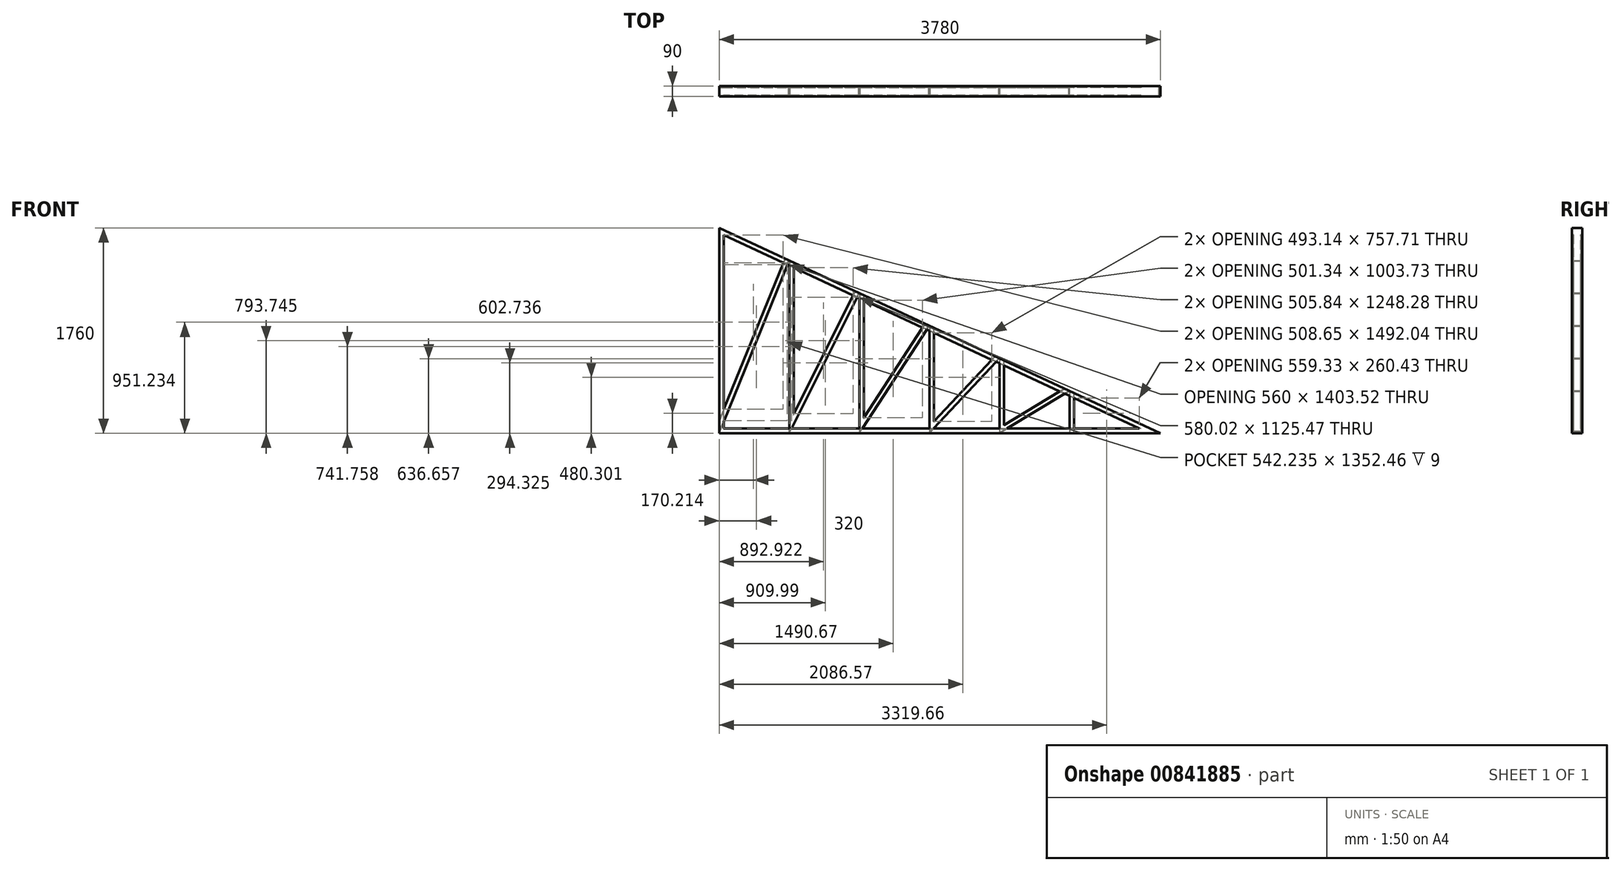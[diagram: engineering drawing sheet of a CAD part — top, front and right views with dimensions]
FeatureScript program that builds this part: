
annotation { "Feature Type Name" : "Feature", "Feature Type Description" : "" }
export const myFeature = defineFeature(function(context is Context, id is Id, definition is map)
    precondition{}
    {
        {
            var Q0;
            Q0=qCreatedBy(makeId("Front.planeOp"),FACE);
            var sketch = newSketch(context, id + "F0", { "sketchPlane" : qUnion([Q0])});
            skLineSegment(sketch, "E0", {"start": v(0, 0) * mm, "end": v(3780, 0) * mm});
            skLineSegment(sketch, "E1", {"start": v(3780, 0) * mm, "end": v(0, 1760) * mm});
            skLineSegment(sketch, "E2", {"start": v(0, 1760) * mm, "end": v(0, 0) * mm});
            skSolve(sketch);
        }
        {
            var Q0;
            Q0=qCreatedBy(makeId("Right.planeOp"),FACE);
            var sketch = newSketch(context, id + "F1", { "sketchPlane" : qUnion([Q0])});
            skLineSegment(sketch, "E3", {"start": v(0, 0) * mm, "end": v(-45, 0) * mm});
            skLineSegment(sketch, "E4", {"start": v(-45, 0) * mm, "end": v(-45, 40) * mm});
            skLineSegment(sketch, "E5", {"start": v(-45, 40) * mm, "end": v(-33, 40) * mm});
            skLineSegment(sketch, "E6.MirrorCS", {"start": v(45, 40) * mm, "end": v(33, 40) * mm});
            skLineSegment(sketch, "E7.MirrorCS", {"start": v(45, 0) * mm, "end": v(45, 40) * mm});
            skLineSegment(sketch, "E8.MirrorCS", {"start": v(0, 0) * mm, "end": v(45, 0) * mm});
            skLineSegment(sketch, "E9.0", {"start": v(-42, 37) * mm, "end": v(-33, 37) * mm});
            skLineSegment(sketch, "E9.1", {"start": v(-42, 3) * mm, "end": v(-42, 37) * mm});
            skLineSegment(sketch, "E9.2", {"start": v(42, 37) * mm, "end": v(33, 37) * mm});
            skLineSegment(sketch, "E9.3", {"start": v(42, 3) * mm, "end": v(42, 37) * mm});
            skLineSegment(sketch, "E9.4", {"start": v(0, 3) * mm, "end": v(42, 3) * mm});
            skLineSegment(sketch, "E9.5", {"start": v(0, 3) * mm, "end": v(-42, 3) * mm});
            skLineSegment(sketch, "E10", {"start": v(33, 40) * mm, "end": v(33, 37) * mm});
            skLineSegment(sketch, "E11", {"start": v(-33, 40) * mm, "end": v(-33, 37) * mm});
            skSolve(sketch);
        }
        {
            var Q0;
            Q0 = qSketchRegion(id + "F1", true);
            var Q1;
            Q1 = qConstructionFilter(qBodyType(qCreatedBy(id + "F0" ,EDGE), BodyType.WIRE), ConstructionObject.NO);
            sweep(context, id + "F2", {"profiles" : qUnion([Q0]), "path" : qUnion([Q1])});
        }
        {
            var Q0;
            Q0=qCreatedBy(makeId("Front.planeOp"),FACE);
            var sketch = newSketch(context, id + "F3", { "sketchPlane" : qUnion([Q0])});
            skLineSegment(sketch, "E12", {"start": v(0, 0) * mm, "end": v(600, 1480.63) * mm});
            skLineSegment(sketch, "E13", {"start": v(600, 1480.63) * mm, "end": v(600, 0) * mm});
            skLineSegment(sketch, "E14", {"start": v(600, 0) * mm, "end": v(1200, 1201.27) * mm});
            skLineSegment(sketch, "E15", {"start": v(1200, 1201.27) * mm, "end": v(1200, 0) * mm});
            skLineSegment(sketch, "E16", {"start": v(1200, 0) * mm, "end": v(1800, 921.9) * mm});
            skLineSegment(sketch, "E17", {"start": v(1800, 921.9) * mm, "end": v(1800, 0) * mm});
            skLineSegment(sketch, "E18", {"start": v(1800, 0) * mm, "end": v(2400, 642.54) * mm});
            skLineSegment(sketch, "E19", {"start": v(2400, 642.54) * mm, "end": v(2400, 0) * mm});
            skLineSegment(sketch, "E20", {"start": v(2400, 0) * mm, "end": v(3000, 363.17) * mm});
            skLineSegment(sketch, "E21", {"start": v(3000, 363.17) * mm, "end": v(3000, 0) * mm});
            skSolve(sketch);
        }
        {
            var Q0;
            Q0=makeQuery(id+"F2.opSweep","CAP_EDGE",EDGE,{"disambiguationData":[OSD([sQuery(id+"F0.wireOp",VERTEX,"E2.end"),sQuery(id+"F1.wireOp",EDGE,"E3"),sQuery(id+"F1.wireOp",EDGE,"E8.MirrorCS")])],"isStart":true});
            cPoint(context, id + "F4", {"entities" : qUnion([Q0]), "parameter" : 0.5});
        }
        {
            var Q0;
            Q0=sQuery(id+"F3.wireOp",EDGE,"E12");
            var Q1;
            Q1 = qCreatedBy(id + "F4" ,VERTEX);
            cPlane(context, id + "F5", {"entities" : qUnion([Q0, Q1]), "cplaneType" : CPlaneType.LINE_POINT, "offset" : 25 * mm, "width" : 150 * mm, "height" : 150 * mm});
        }
        {
            var Q0;
            Q0=qCreatedBy(id+"F5.planeOp",FACE);
            cPlane(context, id + "F6", {"entities" : qUnion([Q0]), "cplaneType" : CPlaneType.OFFSET, "offset" : 125 * mm, "width" : 150 * mm, "height" : 150 * mm});
        }
        {
            var Q0;
            Q0=qCreatedBy(id+"F6.planeOp",FACE);
            var sketch = newSketch(context, id + "F7", { "sketchPlane" : qUnion([Q0])});
            skLineSegment(sketch, "E22", {"start": v(0, 0) * mm, "end": v(0, -45) * mm});
            skLineSegment(sketch, "E23", {"start": v(0, -45) * mm, "end": v(-40, -45) * mm});
            skLineSegment(sketch, "E24", {"start": v(-40, -45) * mm, "end": v(-40, -33) * mm});
            skLineSegment(sketch, "E25", {"start": v(0, 0) * mm, "end": v(-42.42, 0) * mm, "construction": true});
            skLineSegment(sketch, "E26.MirrorCS", {"start": v(-40, 45) * mm, "end": v(-40, 33) * mm});
            skLineSegment(sketch, "E27.MirrorCS", {"start": v(0, 45) * mm, "end": v(-40, 45) * mm});
            skLineSegment(sketch, "E28.MirrorCS", {"start": v(0, 0) * mm, "end": v(0, 45) * mm});
            skLineSegment(sketch, "E29.0", {"start": v(-37, -42) * mm, "end": v(-37, -33) * mm});
            skLineSegment(sketch, "E29.1", {"start": v(-3, -42) * mm, "end": v(-37, -42) * mm});
            skLineSegment(sketch, "E29.2", {"start": v(-37, 42) * mm, "end": v(-37, 33) * mm});
            skLineSegment(sketch, "E29.3", {"start": v(-3, 42) * mm, "end": v(-37, 42) * mm});
            skLineSegment(sketch, "E29.4", {"start": v(-3, 0) * mm, "end": v(-3, 42) * mm});
            skLineSegment(sketch, "E29.5", {"start": v(-3, 0) * mm, "end": v(-3, -42) * mm});
            skLineSegment(sketch, "E30", {"start": v(-40, -33) * mm, "end": v(-37, -33) * mm});
            skLineSegment(sketch, "E31", {"start": v(-40, 33) * mm, "end": v(-37, 33) * mm});
            skSolve(sketch);
        }
        {
            var Q0;
            Q0 = qSketchRegion(id + "F7", true);
            var Q1;
            Q1 = qConstructionFilter(qBodyType(qCreatedBy(id + "F3" ,EDGE), BodyType.WIRE), ConstructionObject.NO);
            sweep(context, id + "F8", {"operationType" : NewBodyOperationType.ADD, "profiles" : qUnion([Q0]), "path" : qUnion([Q1])});
        }
        {
            var Q0;
            {var subQ0=sQuery(id+"F3.wireOp",EDGE,"E12");var subQ2=sQuery(id+"F1.wireOp",EDGE,"E3");var subQ3=sQuery(id+"F0.wireOp",EDGE,"E1");var subQ4=sQuery(id+"F1.wireOp",EDGE,"E4");Q0=makeQuery(id+"F8.boolean.opBoolean","SPLIT",EDGE,{"disambiguationData":[TD([makeQuery(id+"F8.opSweep","SWEPT_FACE",FACE,{"disambiguationData":[OSD([subQ0,sQuery(id+"F7.wireOp",EDGE,"E24")])]})])],"derivedFrom":makeQuery(id+"F2.opSweep","SWEPT_EDGE",EDGE,{"disambiguationData":[OSD([subQ3,subQ2,subQ4])]})});}
            var Q1;
            Q1=makeQuery(id+"F2.opSweep","MID_CAP_VERTEX",VERTEX,{"disambiguationData":[OSD([sQuery(id+"F0.wireOp",EDGE,"E1"),sQuery(id+"F1.wireOp",EDGE,"E3"),sQuery(id+"F1.wireOp",EDGE,"E4")])],"capPos":2.0});
            cPlane(context, id + "F9", {"entities" : qUnion([Q0, Q1]), "cplaneType" : CPlaneType.LINE_POINT, "offset" : 25 * mm, "width" : 150 * mm, "height" : 150 * mm});
        }
        {
            var Q0;
            Q0=qCreatedBy(id+"F9.planeOp",FACE);
            var sketch = newSketch(context, id + "F10", { "sketchPlane" : qUnion([Q0])});
            skLineSegment(sketch, "E32.bottom", {"start": v(45, 1595.53) * mm, "end": v(-60.23, 1595.53) * mm});
            skLineSegment(sketch, "E32.top", {"start": v(45, 1811.1) * mm, "end": v(-60.23, 1811.1) * mm});
            skLineSegment(sketch, "E32.left", {"start": v(45, 1595.53) * mm, "end": v(45, 1811.1) * mm});
            skLineSegment(sketch, "E32.right", {"start": v(-60.23, 1595.53) * mm, "end": v(-60.23, 1811.1) * mm});
            skSolve(sketch);
        }
        {
            var Q0;
            Q0 = qSketchRegion(id + "F10", true);
            extrude(context, id + "F11", {"entities" : qUnion([Q0]), "operationType" : NewBodyOperationType.REMOVE, "endBound" : BoundingType.THROUGH_ALL, "oppositeDirection" : true, "depth" : 25 * mm, "offsetDistance" : 25 * mm});
        }
        {
            var Q0;
            Q0=makeQuery(id+"F2.opSweep","SWEPT_FACE",FACE,{"disambiguationData":[OSD([sQuery(id+"F0.wireOp",EDGE,"E0"),sQuery(id+"F1.wireOp",EDGE,"E3"),sQuery(id+"F1.wireOp",EDGE,"E8.MirrorCS")])]});
            var sketch = newSketch(context, id + "F12", { "sketchPlane" : qUnion([Q0])});
            skLineSegment(sketch, "E33.bottom", {"start": v(0, 45) * mm, "end": v(-59.9, 45) * mm});
            skLineSegment(sketch, "E33.top", {"start": v(0, -50.36) * mm, "end": v(-59.9, -50.36) * mm});
            skLineSegment(sketch, "E33.left", {"start": v(0, 45) * mm, "end": v(0, -50.36) * mm});
            skLineSegment(sketch, "E33.right", {"start": v(-59.9, 45) * mm, "end": v(-59.9, -50.36) * mm});
            skSolve(sketch);
        }
        {
            var Q0;
            Q0 = qSketchRegion(id + "F12", true);
            extrude(context, id + "F13", {"entities" : qUnion([Q0]), "operationType" : NewBodyOperationType.REMOVE, "endBound" : BoundingType.THROUGH_ALL, "oppositeDirection" : true, "depth" : 25 * mm, "offsetDistance" : 25 * mm});
        }
    });
